# Revit family: Kone ECO3000 Escalator New
name_source: partatom
category: Generic Models
revit_build: Autodesk Revit Architecture 2012 (Build: 20110309_2315(x64)
units: mm (PartAtom-declared; Revit-internal decimal feet)

## types (2) — shared parameters
Handrail material = <By Category>
Handrail panel material = Glass
Truss material = <By Category>

## per-type parameters (varying)
| type | A_Run | Bottom Width | Clear width | Finished Width | H_Rise | NumRisers | Step material | Top Width |
| 14.5m | 25115 mm | 2194 mm | 1408 mm  [stored 4.61942 ft] | 2000 mm  [stored 6.56168 ft] | 14500 mm  [stored 47.5722 ft] | 63 | <By Category> | 2603 mm |
| 3.5m | 9163 mm | 2550 mm  [stored 8.36614 ft] | 1100 mm | 1692 mm  [stored 5.55118 ft] | 5290 mm  [stored 17.3556 ft] | 23 | Escalator Steps | 3300 mm  [stored 10.8268 ft] |

note: [stored X ft] marks values corroborated as IEEE doubles in the binary element streams (Revit-internal decimal feet)

## geometry (parser evidence)
native form markers: Sweep x3
no freeform markers — native parametric forms only
